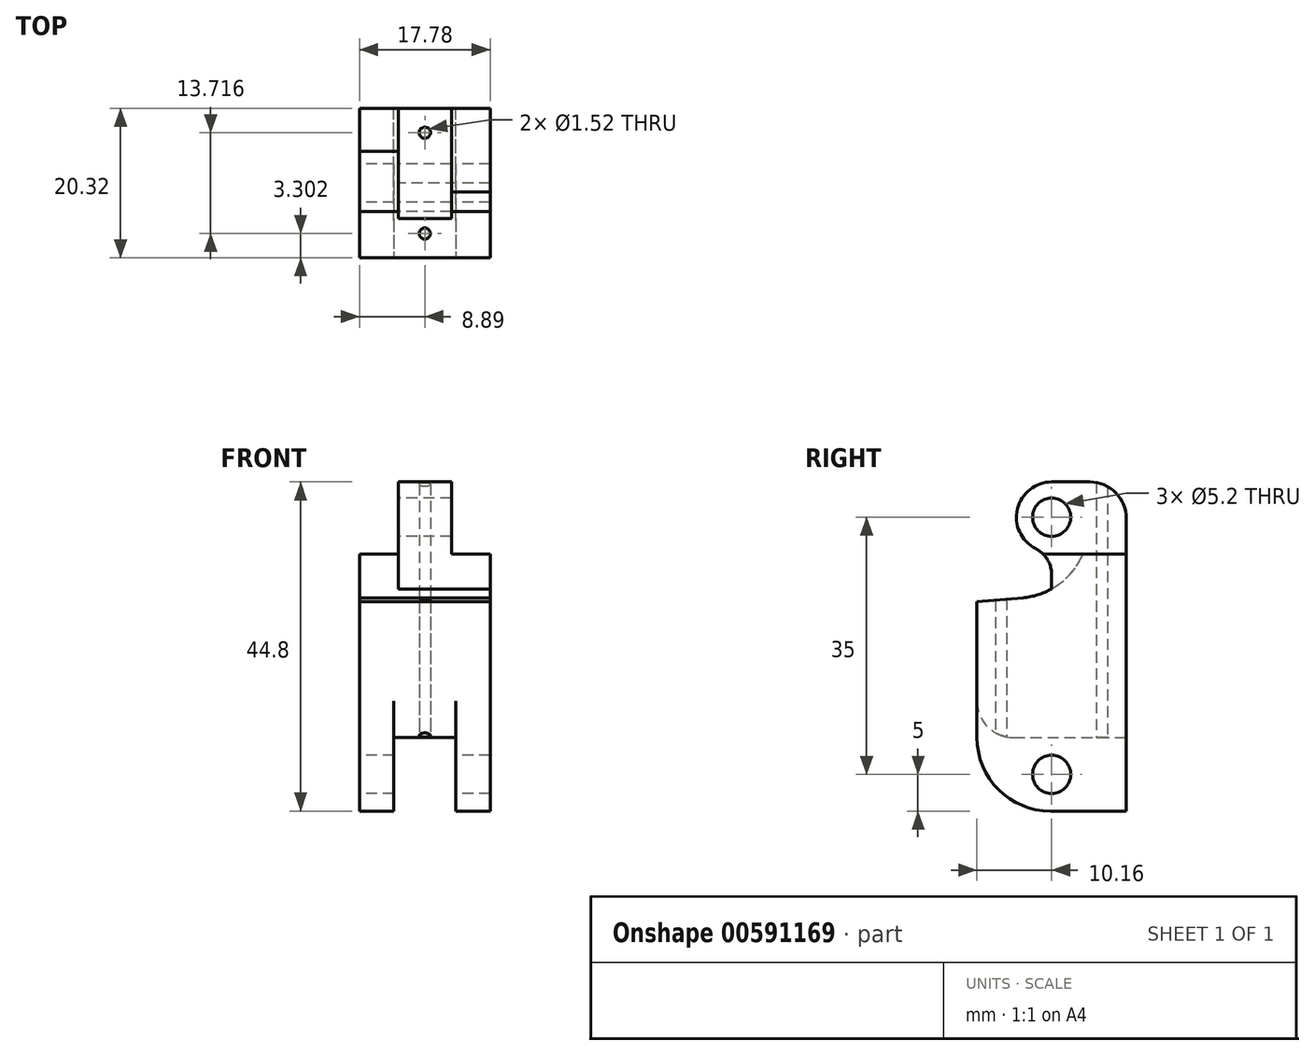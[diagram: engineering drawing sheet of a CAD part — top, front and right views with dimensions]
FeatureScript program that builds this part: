
annotation { "Feature Type Name" : "Feature", "Feature Type Description" : "" }
export const myFeature = defineFeature(function(context is Context, id is Id, definition is map)
    precondition{}
    {
        {
            var Q0;
            Q0=qCreatedBy(makeId("Front.planeOp"),FACE);
            var sketch = newSketch(context, id + "F0", { "sketchPlane" : qUnion([Q0])});
            skLineSegment(sketch, "E0.bottom", {"start": v(8.9, 17.5) * mm, "end": v(3.61, 17.5) * mm});
            skLineSegment(sketch, "E0.top", {"start": v(8.9, -17.5) * mm, "end": v(4.21, -17.5) * mm});
            skLineSegment(sketch, "E0.left", {"start": v(8.89, 17.5) * mm, "end": v(8.89, -17.5) * mm});
            skLineSegment(sketch, "E0.right", {"start": v(-8.9, 17.5) * mm, "end": v(-8.9, -17.5) * mm});
            skPoint(sketch, "E0.middle", {"position": v(0, 0) * mm});
            skLineSegment(sketch, "E1.left", {"start": v(4.21, -17.5) * mm, "end": v(4.21, -7.5) * mm});
            skLineSegment(sketch, "E1.right", {"start": v(-4.21, -17.5) * mm, "end": v(-4.21, -7.5) * mm});
            skLineSegment(sketch, "E2", {"start": v(0, -7.5) * mm, "end": v(4.21, -7.5) * mm});
            skLineSegment(sketch, "E3", {"start": v(0, -7.5) * mm, "end": v(-4.21, -7.5) * mm});
            skLineSegment(sketch, "E4.trimOffspring", {"start": v(-4.21, -17.5) * mm, "end": v(-8.9, -17.5) * mm});
            skLineSegment(sketch, "E5.bottom", {"start": v(3.6, 27.3) * mm, "end": v(-3.61, 27.3) * mm});
            skLineSegment(sketch, "E5.left", {"start": v(3.6, 27.3) * mm, "end": v(3.6, 17.5) * mm});
            skLineSegment(sketch, "E5.right", {"start": v(-3.61, 27.3) * mm, "end": v(-3.61, 17.5) * mm});
            skPoint(sketch, "E5.middle", {"position": v(0, 17.5) * mm});
            skLineSegment(sketch, "E6.trimOffspring", {"start": v(-3.61, 17.5) * mm, "end": v(-8.9, 17.5) * mm});
            skPoint(sketch, "E7.orphan", {"position": v(-3.6, 7.7) * mm});
            skPoint(sketch, "E8.orphan", {"position": v(3.6, 7.7) * mm});
            skSolve(sketch);
        }
        {
            var Q0;
            Q0=makeQuery(id+"F0.imprint","IMPRINT",FACE,{"disambiguationData":[TD([[makeQuery(id+"F0.imprint","IMPRINT",EDGE,{"derivedFrom":sQuery(id+"F0.wireOp",EDGE,"E0.bottom")}),1.0]])]});
            extrude(context, id + "F1", {"entities" : qUnion([Q0]), "depth" : 20.32 * mm, "offsetDistance" : 25.4 * mm, "symmetric" : true});
        }
        {
            var Q0;
            Q0=makeQuery(id+"F1.opExtrude","SWEPT_FACE",FACE,{"disambiguationData":[OSD([sQuery(id+"F0.wireOp",EDGE,"E0.right")])]});
            var sketch = newSketch(context, id + "F2", { "sketchPlane" : qUnion([Q0])});
            skPoint(sketch, "E9.endSnap0", {"position": v(0, -17.5) * mm});
            skCircle(sketch, "E10", {"center": v(0, -12.5) * mm, "radius": 2.6 * mm});
            skSolve(sketch);
        }
        {
            var Q0;
            Q0=makeQuery(id+"F2.imprint","IMPRINT",FACE,{"disambiguationData":[TD([[makeQuery(id+"F2.imprint","IMPRINT",EDGE,{"derivedFrom":sQuery(id+"F2.wireOp",EDGE,"E10")}),1.0]])]});
            extrude(context, id + "F3", {"entities" : qUnion([Q0]), "operationType" : NewBodyOperationType.REMOVE, "endBound" : BoundingType.THROUGH_ALL, "oppositeDirection" : true, "depth" : 25.4 * mm, "offsetDistance" : 25.4 * mm});
        }
        {
            var Q0;
            Q0=makeQuery(id+"F1.opExtrude","SWEPT_FACE",FACE,{"disambiguationData":[OSD([sQuery(id+"F0.wireOp",EDGE,"E0.right")])]});
            var sketch = newSketch(context, id + "F4", { "sketchPlane" : qUnion([Q0])});
            skLineSegment(sketch, "E11", {"start": v(10.16, 17.5) * mm, "end": v(-4.3, 17.5) * mm});
            skLineSegment(sketch, "E12", {"start": v(10.16, 17.5) * mm, "end": v(10.16, 10.97) * mm});
            skLineSegment(sketch, "E13", {"start": v(10.16, 10.97) * mm, "end": v(3.89, 11.52) * mm});
            skPoint(sketch, "E14.visualSharp", {"position": v(-2.14, 14.35) * mm});
            skArc(sketch, "E14.filletArc", {"start": v(-4.3, 17.5) * mm, "mid": v(-1.02, 13.4) * mm, "end": v(3.89, 11.52) * mm});
            skSolve(sketch);
        }
        {
            var Q0;
            Q0=makeQuery(id+"F4.imprint","IMPRINT",FACE,{"disambiguationData":[TD([[makeQuery(id+"F4.imprint","IMPRINT",EDGE,{"derivedFrom":sQuery(id+"F4.wireOp",EDGE,"E11")}),1.0]])]});
            extrude(context, id + "F5", {"entities" : qUnion([Q0]), "operationType" : NewBodyOperationType.REMOVE, "oppositeDirection" : true, "depth" : 5.08 * mm + .2 * mm, "offsetDistance" : 25.4 * mm});
        }
        {
            var Q0;
            Q0=makeQuery(id+"F1.opExtrude","CAP_EDGE",EDGE,{"disambiguationData":[OSD([sQuery(id+"F0.wireOp",EDGE,"E0.top")])],"isStart":false});
            var Q1;
            Q1=makeQuery(id+"F1.opExtrude","CAP_EDGE",EDGE,{"disambiguationData":[OSD([sQuery(id+"F0.wireOp",EDGE,"E4.trimOffspring")])],"isStart":false});
            fillet(context, id + "F6", {"entities" : qUnion([Q0, Q1]), "radius" : 10 * mm, "tangentPropagation" : true, "allowEdgeOverflow" : false});
        }
        {
            var Q0;
            Q0=makeQuery(id+"F5.boolean.opBoolean","MERGE",FACE,{"derivedFrom":[makeQuery(id+"F1.opExtrude","SWEPT_FACE",FACE,{"disambiguationData":[OSD([sQuery(id+"F0.wireOp",EDGE,"E5.right")])]}),makeQuery(id+"F5.opExtrude","CAP_FACE",FACE,{"disambiguationData":[OSD([sQuery(id+"F4.wireOp",EDGE,"E11"),sQuery(id+"F4.wireOp",EDGE,"E12"),sQuery(id+"F4.wireOp",EDGE,"E13"),sQuery(id+"F4.wireOp",EDGE,"E14.filletArc")])],"isStart":false})]});
            var sketch = newSketch(context, id + "F7", { "sketchPlane" : qUnion([Q0])});
            skLineSegment(sketch, "E15", {"start": v(0, 17.5) * mm, "end": v(0, 17.7) * mm});
            skCircle(sketch, "E16", {"center": v(0, 22.5) * mm, "radius": 2.6 * mm});
            skArc(sketch, "E17", {"start": v(0, 17.7) * mm, "mid": v(4.8, 22.5) * mm, "end": v(0, 27.3) * mm});
            skLineSegment(sketch, "E18", {"start": v(0, 27.3) * mm, "end": v(10.16, 27.3) * mm});
            skLineSegment(sketch, "E19", {"start": v(10.16, 27.3) * mm, "end": v(10.16, 10.97) * mm});
            skLineSegment(sketch, "E20", {"start": v(0, 17.5) * mm, "end": v(0, 12.75) * mm});
            skArc(sketch, "E21", {"start": v(0, 12.75) * mm, "mid": v(2, 11.9) * mm, "end": v(4.14, 11.5) * mm});
            skPoint(sketch, "E21.first.point", {"position": v(-4.3, 17.5) * mm});
            skPoint(sketch, "E21.third.point", {"position": v(13.07, 27.21) * mm});
            skLineSegment(sketch, "E22", {"start": v(10.16, 10.97) * mm, "end": v(3.89, 11.52) * mm});
            skArc(sketch, "E23.trimOffspring", {"start": v(-4.3, 17.5) * mm, "mid": v(-1.02, 13.4) * mm, "end": v(3.89, 11.52) * mm});
            skSolve(sketch);
        }
        {
            var Q0;
            Q0=makeQuery(id+"F7.imprint","IMPRINT",FACE,{"disambiguationData":[TD([[makeQuery(id+"F7.imprint","IMPRINT",EDGE,{"derivedFrom":sQuery(id+"F7.wireOp",EDGE,"E16")}),1.0]])]});
            var Q1;
            Q1=makeQuery(id+"F7.imprint","IMPRINT",FACE,{"disambiguationData":[TD([[makeQuery(id+"F7.imprint","IMPRINT",EDGE,{"derivedFrom":sQuery(id+"F7.wireOp",EDGE,"E15")}),-1.0]])]});
            extrude(context, id + "F8", {"entities" : qUnion([Q0, Q1]), "operationType" : NewBodyOperationType.REMOVE, "endBound" : BoundingType.THROUGH_ALL, "oppositeDirection" : true, "depth" : 25.4 * mm, "offsetDistance" : 25.4 * mm});
        }
        {
            var Q0;
            Q0=makeQuery(id+"F8.boolean.opBoolean","COPY",EDGE,{"derivedFrom":makeQuery(id+"F8.opExtrude","SWEPT_EDGE",EDGE,{"disambiguationData":[OSD([sQuery(id+"F7.wireOp",EDGE,"E15"),sQuery(id+"F7.wireOp",EDGE,"E17")])]})});
            var Q1;
            Q1=makeQuery(id+"F8.boolean.opBoolean","COPY",EDGE,{"derivedFrom":makeQuery(id+"F8.opExtrude","SWEPT_EDGE",EDGE,{"disambiguationData":[OSD([sQuery(id+"F7.wireOp",EDGE,"E20"),sQuery(id+"F7.wireOp",EDGE,"E22")])]})});
            fillet(context, id + "F9", {"entities" : qUnion([Q0, Q1]), "radius" : 4 * mm, "tangentPropagation" : true, "allowEdgeOverflow" : false});
        }
        {
            var Q0;
            Q0=makeQuery(id+"F1.opExtrude","CAP_EDGE",EDGE,{"disambiguationData":[OSD([sQuery(id+"F0.wireOp",EDGE,"E5.bottom")])],"isStart":true});
            fillet(context, id + "F10", {"entities" : qUnion([Q0]), "radius" : 5 * mm, "tangentPropagation" : true, "allowEdgeOverflow" : false});
        }
        {
            var Q0;
            Q0=makeQuery(id+"F1.opExtrude","CAP_EDGE",EDGE,{"disambiguationData":[OSD([sQuery(id+"F0.wireOp",EDGE,"E2"),sQuery(id+"F0.wireOp",EDGE,"E3")])],"isStart":false});
            fillet(context, id + "F11", {"entities" : qUnion([Q0]), "radius" : 5 * mm, "tangentPropagation" : true, "allowEdgeOverflow" : false});
        }
        {
            var Q0;
            Q0=makeQuery(id+"F1.opExtrude","SWEPT_FACE",FACE,{"disambiguationData":[OSD([sQuery(id+"F0.wireOp",EDGE,"E2"),sQuery(id+"F0.wireOp",EDGE,"E3")])]});
            var sketch = newSketch(context, id + "F12", { "sketchPlane" : qUnion([Q0])});
            skLineSegment(sketch, "E24", {"start": v(0, -10.16) * mm, "end": v(0, -7.62) * mm});
            skPoint(sketch, "E24.endSnap0", {"position": v(0, -10.16) * mm});
            skCircle(sketch, "E25", {"center": v(0, -6.86) * mm, "radius": 0.76 * mm});
            skLineSegment(sketch, "E26", {"start": v(0, 10.16) * mm, "end": v(0, 7.62) * mm});
            skCircle(sketch, "E27", {"center": v(0, 6.86) * mm, "radius": 0.76 * mm});
            skLineSegment(sketch, "E28", {"start": v(-8.9, 10.16) * mm, "end": v(8.89, 10.16) * mm});
            skSolve(sketch);
        }
        {
            var Q0;
            Q0=makeQuery(id+"F12.imprint","IMPRINT",FACE,{"disambiguationData":[TD([[makeQuery(id+"F12.imprint","IMPRINT",EDGE,{"derivedFrom":sQuery(id+"F12.wireOp",EDGE,"E27")}),1.0]])]});
            var Q1;
            Q1=makeQuery(id+"F12.imprint","IMPRINT",FACE,{"disambiguationData":[TD([[makeQuery(id+"F12.imprint","IMPRINT",EDGE,{"derivedFrom":sQuery(id+"F12.wireOp",EDGE,"E25")}),1.0]])]});
            extrude(context, id + "F13", {"entities" : qUnion([Q0, Q1]), "operationType" : NewBodyOperationType.REMOVE, "endBound" : BoundingType.THROUGH_ALL, "oppositeDirection" : true, "depth" : 25.4 * mm, "offsetDistance" : 25.4 * mm});
        }
    });
